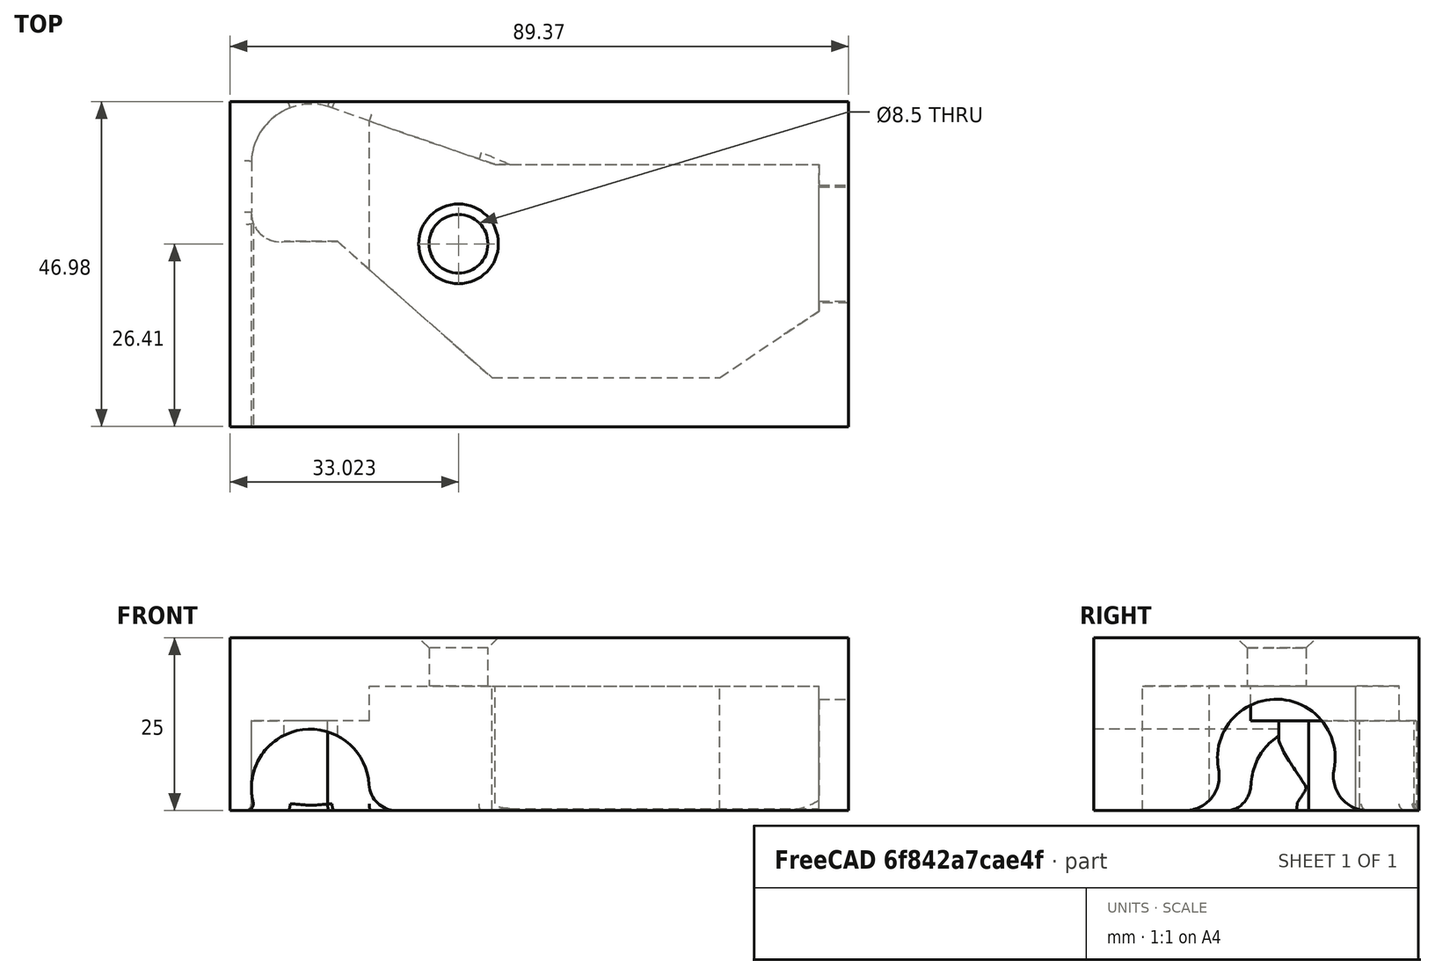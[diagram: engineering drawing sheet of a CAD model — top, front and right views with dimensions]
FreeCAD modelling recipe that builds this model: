
FCSTD DOCUMENT  (FreeCAD 0.17R9537 (Git))
Label: y_corner_right_insert_jig
License: All rights reserved
LicenseURL: http://en.wikipedia.org/wiki/All_rights_reserved
objects: Sketcher::SketchObject×8, PartDesign::Pocket×5, PartDesign::Fillet×3, Part::Feature×2, Mesh::Feature×1, PartDesign::Pad×1, PartDesign::Plane×1, PartDesign::Chamfer×1, PartDesign::Body×1, Part::Mirroring×1, Part::Part2DObjectPython×1
note: 30 computed .brp shape members not serialized (recipe doc carries the construction recipe); baked Part::Feature solids carry a one-line shape summary decoded from their .brp

FEATURE [Mesh::Feature] y_corner_left_v2_4  label="y_corner_left_v2.4"
  Placement = pos=(-95,-15,-13) rot=(0,0,1;0rad)
FEATURE [Sketcher::SketchObject] Sketch
  MapMode = 5
  Support = -> [XY_Plane]
  sketch-geometry (4):
    g0: LineSegment StartX=-41.2454 StartY=-29.3641 StartZ=0 EndX=48.1248 EndY=-29.3641 EndZ=0
    g1: LineSegment StartX=48.1248 StartY=-29.3641 StartZ=0 EndX=48.1248 EndY=17.6233 EndZ=0
    g2: LineSegment StartX=48.1248 StartY=17.6233 StartZ=0 EndX=-41.2454 EndY=17.6233 EndZ=0
    g3: LineSegment StartX=-41.2454 StartY=17.6233 StartZ=0 EndX=-41.2454 EndY=-29.3641 EndZ=0
  constraints (8):
    c: Coincident(g0,g1)
    c: Coincident(g1,g2)
    c: Coincident(g2,g3)
    c: Coincident(g3,g0)
    c: Horizontal(g0)
    c: Horizontal(g2)
    c: Vertical(g1)
    c: Vertical(g3)
FEATURE [PartDesign::Pad] Pad
  Length = 25
  Length2 = 100
  Profile = -> Sketch
  Type = 0
FEATURE [Part::Feature] y_corner_left_v2_4001
  Placement = pos=(0,0,12) rot=(0,0,1;0rad)
  shape: bbox 81.06 x 37.98 x 18.29 mm, 18592 faces, 0 solids (baked)
FEATURE [Sketcher::SketchObject] Sketch001
  MapMode = 5
  Placement = pos=(0,0,0) rot=(1,0,0;3.14159rad)
  Support = -> [Pad]
  sketch-geometry (7):
    g0: LineSegment StartX=-21.1438 StartY=5.05934 StartZ=0 EndX=-3.38972 EndY=-10.5427 EndZ=0
    g1: LineSegment StartX=-3.38972 StartY=-10.5427 StartZ=0 EndX=29.5098 EndY=-10.5427 EndZ=0
    g2: LineSegment StartX=29.5098 StartY=-10.5427 StartZ=0 EndX=43.8429 EndY=-0.932231 EndZ=0
    g3: LineSegment StartX=43.8429 StartY=-0.932231 StartZ=0 EndX=43.8429 EndY=20.2526 EndZ=0
    g4: LineSegment StartX=-21.1438 StartY=5.05934 StartZ=0 EndX=-21.1438 EndY=26.5193 EndZ=0
    g5: LineSegment StartX=-21.1438 StartY=26.5193 StartZ=0 EndX=-2.94605 EndY=20.2526 EndZ=0
    g6: LineSegment StartX=-2.94605 StartY=20.2526 StartZ=0 EndX=43.8429 EndY=20.2526 EndZ=0
  constraints (11):
    c: Coincident(g1,g0)
    c: Horizontal(g1)
    c: Coincident(g2,g1)
    c: Coincident(g3,g2)
    c: Vertical(g3)
    c: Coincident(g4,g0)
    c: Vertical(g4)
    c: Coincident(g5,g4)
    c: Coincident(g6,g5)
    c: Coincident(g6,g3)
    c: Horizontal(g6)
FEATURE [PartDesign::Pocket] Pocket
  BaseFeature = -> Pad
  Length = 18
  Profile = -> Sketch001
  Type = 0
FEATURE [Sketcher::SketchObject] Sketch002
  ExternalGeometry = -> [Pocket]
  MapMode = 5
  Placement = pos=(0,0,0) rot=(1,0,0;3.14159rad)
  Support = -> [Pocket]
  sketch-geometry (7):
    g0: LineSegment StartX=-21.1438 StartY=5.05934 StartZ=0 EndX=-25.6743 EndY=9.11448 EndZ=0
    g1: LineSegment StartX=-25.6743 StartY=9.11448 StartZ=0 EndX=-33.4497 EndY=9.11448 EndZ=0
    g2: LineSegment StartX=-21.1438 StartY=26.5193 StartZ=0 EndX=-27.1407 EndY=28.6513 EndZ=0
    g3: ArcOfCircle CenterX=-29.5136 CenterY=20.3238 CenterZ=0 NormalX=0 NormalY=0 NormalZ=1 Radius=8.65904 StartAngle=1.2932 EndAngle=3.08945
    g4: LineSegment StartX=-38.1609 StartY=20.7751 StartZ=0 EndX=-38.1609 EndY=13.4153 EndZ=0
    g5: ArcOfCircle CenterX=-33.9785 CenterY=13.266 CenterZ=0 NormalX=0 NormalY=0 NormalZ=1 Radius=4.18506 StartAngle=3.10591 EndAngle=4.83908
    g6: LineSegment StartX=-21.1438 StartY=5.05934 StartZ=0 EndX=-21.1438 EndY=26.5193 EndZ=0
  constraints (11):
    c: Coincident(g0,g-3)
    c: Coincident(g1,g0)
    c: Horizontal(g1)
    c: Coincident(g2,g-3)
    c: Coincident(g3,g2)
    c: Coincident(g4,g3)
    c: Vertical(g4)
    c: Coincident(g1,g5)
    c: Coincident(g4,g5)
    c: Coincident(g6,g0)
    c: Coincident(g6,g2)
FEATURE [PartDesign::Pocket] Pocket001
  BaseFeature = -> Pocket
  Length = 13
  Profile = -> Sketch002
  Type = 0
FEATURE [Sketcher::SketchObject] Sketch003
  MapMode = 5
  Placement = pos=(0,17.6233,0) rot=(0,0.707107,0.707107;3.14159rad)
  Support = -> [Pocket001]
  sketch-geometry (1):
    g0: Circle CenterX=29.6574 CenterY=3.27274 CenterZ=0 NormalX=0 NormalY=0 NormalZ=1 Radius=8.5
  constraints (1):
    c: Radius(g0) = 8.5
FEATURE [PartDesign::Pocket] Pocket002
  BaseFeature = -> Pocket001
  Length = 35
  Profile = -> Sketch003
  Type = 0
FEATURE [Sketcher::SketchObject] Sketch004
  MapMode = 5
  Placement = pos=(48.1248,0,0) rot=(0.57735,0.57735,0.57735;2.0944rad)
  Support = -> [Pocket002]
  sketch-geometry (1):
    g0: Circle CenterX=-8.75085 CenterY=7.61123 CenterZ=0 NormalX=0 NormalY=0 NormalZ=1 Radius=8.5
  constraints (1):
    c: Radius(g0) = 8.5
FEATURE [PartDesign::Pocket] Pocket003
  BaseFeature = -> Pocket002
  Length = 5
  Profile = -> Sketch004
  Type = 0
FEATURE [PartDesign::Fillet] Fillet
  Base = -> Pocket003 [Edge31,Edge23]
  BaseFeature = -> Pocket003
  Radius = 5
FEATURE [PartDesign::Fillet] Fillet001
  Base = -> Fillet [Edge43]
  BaseFeature = -> Fillet
  Radius = 4
FEATURE [PartDesign::Fillet] Fillet002
  Base = -> Fillet001 [Edge32,Edge41,Edge40,Edge38,Edge37,Edge35]
  BaseFeature = -> Fillet001
  Radius = 1
FEATURE [Sketcher::SketchObject] Sketch005
  ExternalGeometry = -> [y_corner_left_v2_4001,Fillet002]
  MapMode = 5
  Placement = pos=(0,-29.3641,0) rot=(1,0,0;1.5708rad)
  Support = -> [Fillet002]
  sketch-geometry (1):
    g0: LineSegment StartX=-26.1602 StartY=0 StartZ=0 EndX=-26.1602 EndY=-0.999892 EndZ=0
  constraints (3):
    c: Coincident(g0,g-4)
    c: PointOnObject(g0,g-3)
    c: Vertical(g0)
FEATURE [Sketcher::SketchObject] Sketch006
  MapMode = 5
  Placement = pos=(0,0,18) rot=(1,0,0;3.14159rad)
  Support = -> [Fillet002]
  sketch-geometry (1):
    g0: Circle CenterX=-8.22724 CenterY=8.79045 CenterZ=0 NormalX=0 NormalY=0 NormalZ=1 Radius=4.25
  constraints (1):
    c: Radius(g0) = 4.25
FEATURE [PartDesign::Pocket] Pocket004
  BaseFeature = -> Fillet002
  Length = 5
  Profile = -> Sketch006
  Type = 1
FEATURE [PartDesign::Plane] DatumPlane
  MapMode = 5
  Placement = pos=(0,0,10) rot=(1,0,0;3.14159rad)
  Support = -> [Pocket004]
  superPlacement = pos=(0,0,-10) rot=(0,0,1;0rad)
FEATURE [Sketcher::SketchObject] Sketch007
  ExternalGeometry = -> [Pocket004]
  MapMode = 5
  Placement = pos=(0,17.6233,0) rot=(0,0.707107,0.707107;3.14159rad)
  Support = -> [Pocket004]
  sketch-geometry (1):
    g0: LineSegment StartX=3.2818 StartY=25 StartZ=0 EndX=3.2818 EndY=9.8977 EndZ=0
  constraints (2):
    c: PointOnObject(g0,g-3)
    c: Vertical(g0)
FEATURE [PartDesign::Chamfer] Chamfer
  Base = -> Pocket004 [Edge37]
  BaseFeature = -> Pocket004
  Size = 1.5
FEATURE [PartDesign::Body] Body
  Model = -> [Sketch,Pad,Sketch001,Pocket,Sketch002,Pocket001,Sketch003,Pocket002,Sketch004,Pocket003,Fillet,Fillet001,Fillet002,Pocket004,DatumPlane,Sketch007,Chamfer]
  Origin = -> BodyOrigin
FEATURE [Part::Mirroring] Part__Mirroring  label="Chamfer (Mirror #1)"
  Base = (0,0,0)
  Normal = (0,1,0)
  Source = -> Chamfer
FEATURE [Part::Part2DObjectPython] ShapeString  # Draft 2D object (typed FeaturePython)
  FontFile = <userpath>/Desktop/Titillium-BoldUpright.otf
  Placement = pos=(-27,21,25) rot=(0,0,1;0rad)
  Size = 2.5
  String = Y Corner Right Insert Jig
  Support = -> [Part__Mirroring]
  Tracking = 70
FEATURE [Part::Feature] Part__Mirroring001  label="Chamfer (Mirror #1)001"
  shape: bbox 89.37 x 47.73 x 25 mm, 41 faces (baked)
